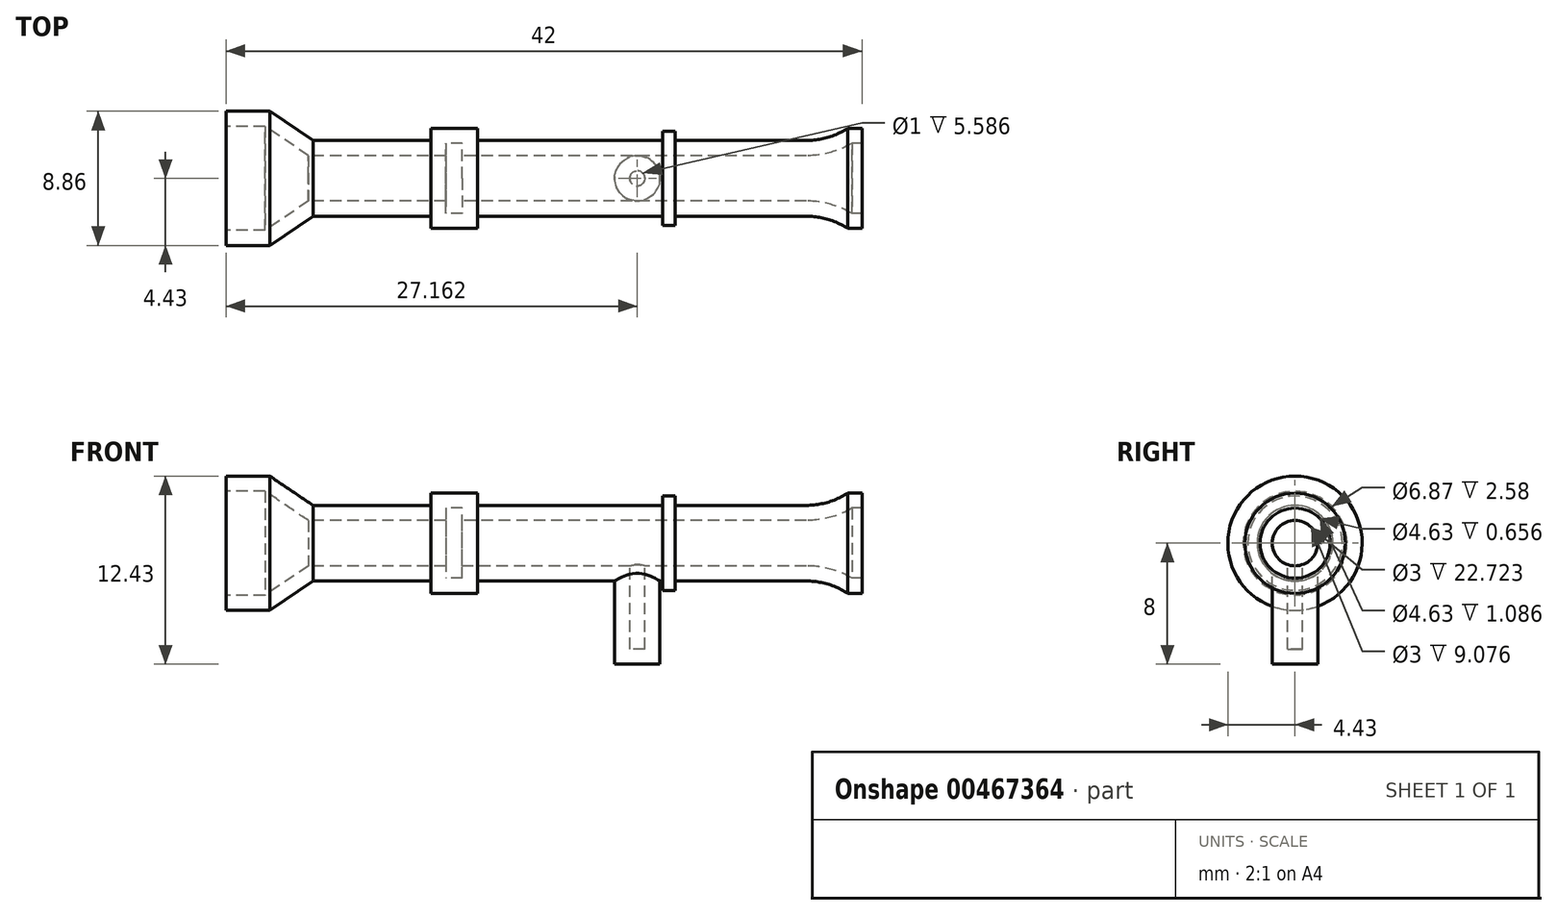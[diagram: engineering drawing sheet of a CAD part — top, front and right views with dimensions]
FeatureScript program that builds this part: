
annotation { "Feature Type Name" : "Feature", "Feature Type Description" : "" }
export const myFeature = defineFeature(function(context is Context, id is Id, definition is map)
    precondition{}
    {
        {
            var Q0;
            Q0=qCreatedBy(makeId("Front.planeOp"),FACE);
            var sketch = newSketch(context, id + "F0", { "sketchPlane" : qUnion([Q0])});
            skLineSegment(sketch, "E0", {"start": v(-42, 0) * mm, "end": v(0, 0) * mm, "construction": true});
            skLineSegment(sketch, "E1", {"start": v(-42, 0) * mm, "end": v(-42, 4.43) * mm});
            skLineSegment(sketch, "E2", {"start": v(-42, 4.43) * mm, "end": v(-39.11, 4.43) * mm});
            skLineSegment(sketch, "E3", {"start": v(-39.11, 4.43) * mm, "end": v(-36.25, 2.5) * mm});
            skLineSegment(sketch, "E4", {"start": v(-36.25, 2.5) * mm, "end": v(-28.48, 2.5) * mm});
            skLineSegment(sketch, "E5", {"start": v(-28.48, 2.5) * mm, "end": v(-28.48, 3.31) * mm});
            skLineSegment(sketch, "E6", {"start": v(-28.48, 3.31) * mm, "end": v(-25.4, 3.31) * mm});
            skLineSegment(sketch, "E7", {"start": v(-25.4, 3.31) * mm, "end": v(-25.4, 2.5) * mm});
            skLineSegment(sketch, "E8", {"start": v(-25.4, 2.5) * mm, "end": v(-13.17, 2.5) * mm});
            skLineSegment(sketch, "E9", {"start": v(-0.94, 2.5) * mm, "end": v(-0.94, 3.31) * mm});
            skLineSegment(sketch, "E10", {"start": v(-0.94, 3.31) * mm, "end": v(0, 3.31) * mm});
            skLineSegment(sketch, "E11", {"start": v(0, 3.31) * mm, "end": v(0, 0) * mm});
            skLineSegment(sketch, "E12", {"start": v(-13.17, 2.5) * mm, "end": v(-13.17, 3.12) * mm});
            skLineSegment(sketch, "E13", {"start": v(-13.17, 3.12) * mm, "end": v(-12.32, 3.12) * mm});
            skLineSegment(sketch, "E14", {"start": v(-12.32, 3.12) * mm, "end": v(-12.32, 2.5) * mm});
            skLineSegment(sketch, "E15.trimOffspring", {"start": v(-12.32, 2.5) * mm, "end": v(-0.94, 2.5) * mm});
            skLineSegment(sketch, "E16", {"start": v(-42, 0) * mm, "end": v(0, 0) * mm});
            skSolve(sketch);
        }
        {
            var Q0;
            Q0=makeQuery(id+"F0.imprint","IMPRINT",FACE,{"disambiguationData":[TD([[makeQuery(id+"F0.imprint","IMPRINT",EDGE,{"derivedFrom":sQuery(id+"F0.wireOp",EDGE,"E1")}),-1.0]])]});
            var Q1;
            Q1=sQuery(id+"F0.wireOp",EDGE,"E16");
            revolve(context, id + "F1", {"entities" : qUnion([Q0]), "axis" : qUnion([Q1]), "revolveType" : RevolveType.FULL});
        }
        {
            var Q0;
            Q0=qCreatedBy(makeId("Top.planeOp"),FACE);
            var sketch = newSketch(context, id + "F2", { "sketchPlane" : qUnion([Q0])});
            skCircle(sketch, "E17", {"center": v(-14.84, 0) * mm, "radius": 1.5 * mm});
            skSolve(sketch);
        }
        {
            var Q0;
            Q0 = qSketchRegion(id + "F2", true);
            extrude(context, id + "F3", {"entities" : qUnion([Q0]), "operationType" : NewBodyOperationType.ADD, "oppositeDirection" : true, "depth" : 8 * mm});
        }
        {
            var Q0;
            Q0=makeQuery(id+"F1.opRevolve","SWEPT_EDGE",EDGE,{"disambiguationData":[OSD([sQuery(id+"F0.wireOp",EDGE,"E9"),sQuery(id+"F0.wireOp",EDGE,"E15.trimOffspring")])]});
            fillet(context, id + "F4", {"entities" : qUnion([Q0]), "radius" : 5 * mm, "tangentPropagation" : true, "allowEdgeOverflow" : false});
        }
        {
            var Q0;
            Q0=makeQuery(id+"F1.opRevolve","SWEPT_FACE",FACE,{"disambiguationData":[OSD([sQuery(id+"F0.wireOp",EDGE,"E1")])]});
            var Q1;
            Q1=makeQuery(id+"F1.opRevolve","SWEPT_FACE",FACE,{"disambiguationData":[OSD([sQuery(id+"F0.wireOp",EDGE,"E11")])]});
            shell(context, id + "F5", {"entities" : qUnion([Q0, Q1]), "thickness" : 1 * mm});
        }
    });
